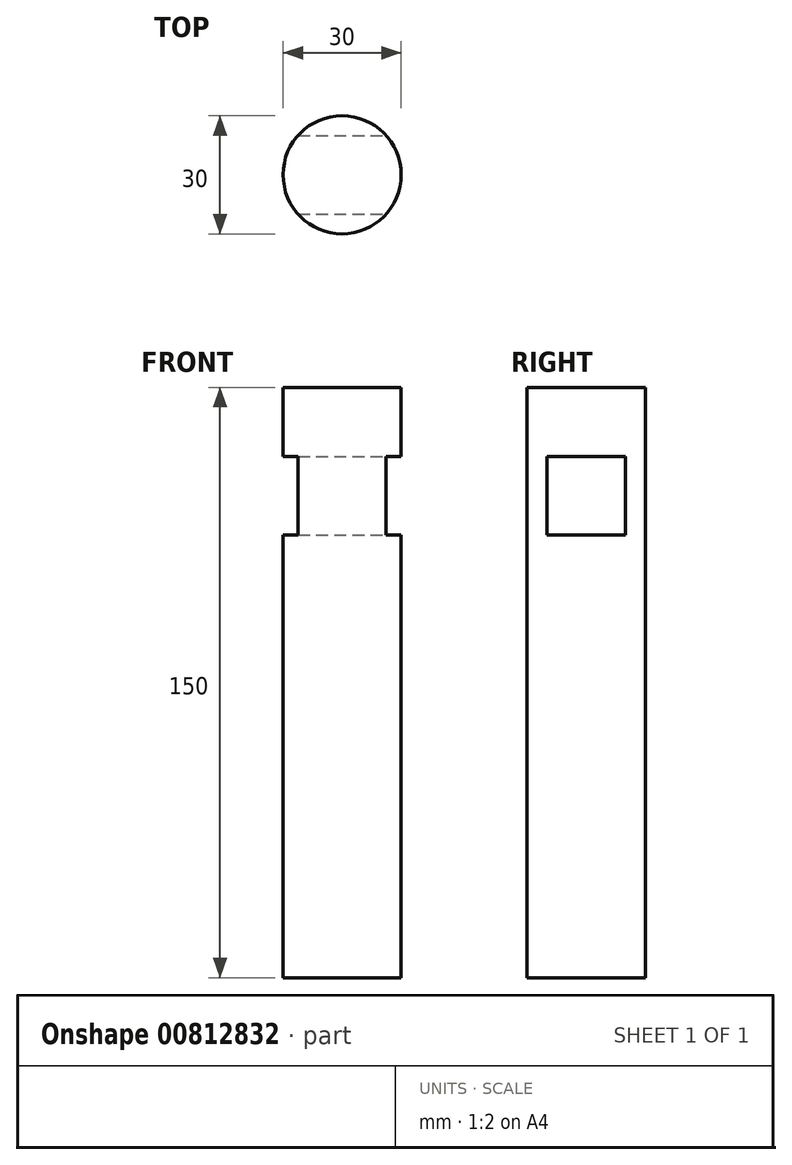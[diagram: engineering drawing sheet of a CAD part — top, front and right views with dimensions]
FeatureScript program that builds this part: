
annotation { "Feature Type Name" : "Feature", "Feature Type Description" : "" }
export const myFeature = defineFeature(function(context is Context, id is Id, definition is map)
    precondition{}
    {
        {
            var Q0;
            Q0=qCreatedBy(makeId("Top.planeOp"),FACE);
            var sketch = newSketch(context, id + "F0", { "sketchPlane" : qUnion([Q0])});
            skCircle(sketch, "E0", {"center": v(0, 0) * mm, "radius": 15 * mm});
            skSolve(sketch);
        }
        {
            var Q0;
            Q0=makeQuery(id+"F0.imprint","IMPRINT",FACE,{"disambiguationData":[TD([[makeQuery(id+"F0.imprint","IMPRINT",EDGE,{"derivedFrom":sQuery(id+"F0.wireOp",EDGE,"E0")}),1.0]])]});
            extrude(context, id + "F1", {"entities" : qUnion([Q0]), "depth" : 150 * mm, "offsetDistance" : 25 * mm});
        }
        {
            var Q0;
            Q0=qCreatedBy(makeId("Right.planeOp"),FACE);
            var sketch = newSketch(context, id + "F2", { "sketchPlane" : qUnion([Q0])});
            skLineSegment(sketch, "E1.bottom", {"start": v(10, 132.48) * mm, "end": v(-10, 132.48) * mm});
            skLineSegment(sketch, "E1.top", {"start": v(10, 112.48) * mm, "end": v(-10, 112.48) * mm});
            skLineSegment(sketch, "E1.left", {"start": v(10, 132.48) * mm, "end": v(10, 112.48) * mm});
            skLineSegment(sketch, "E1.right", {"start": v(-10, 132.48) * mm, "end": v(-10, 112.48) * mm});
            skSolve(sketch);
        }
        {
            var Q0;
            Q0=makeQuery(id+"F2.imprint","IMPRINT",FACE,{"disambiguationData":[TD([[makeQuery(id+"F2.imprint","IMPRINT",EDGE,{"derivedFrom":sQuery(id+"F2.wireOp",EDGE,"E1.bottom")}),1.0]])]});
            extrude(context, id + "F3", {"entities" : qUnion([Q0]), "operationType" : NewBodyOperationType.REMOVE, "endBound" : BoundingType.UP_TO_NEXT, "oppositeDirection" : true, "depth" : 50 * mm, "offsetDistance" : 25 * mm, "hasSecondDirection" : true, "secondDirectionBound" : SecondDirectionBoundingType.UP_TO_NEXT, "secondDirectionOppositeDirection" : false, "secondDirectionDepth" : 50 * mm});
        }
    });
